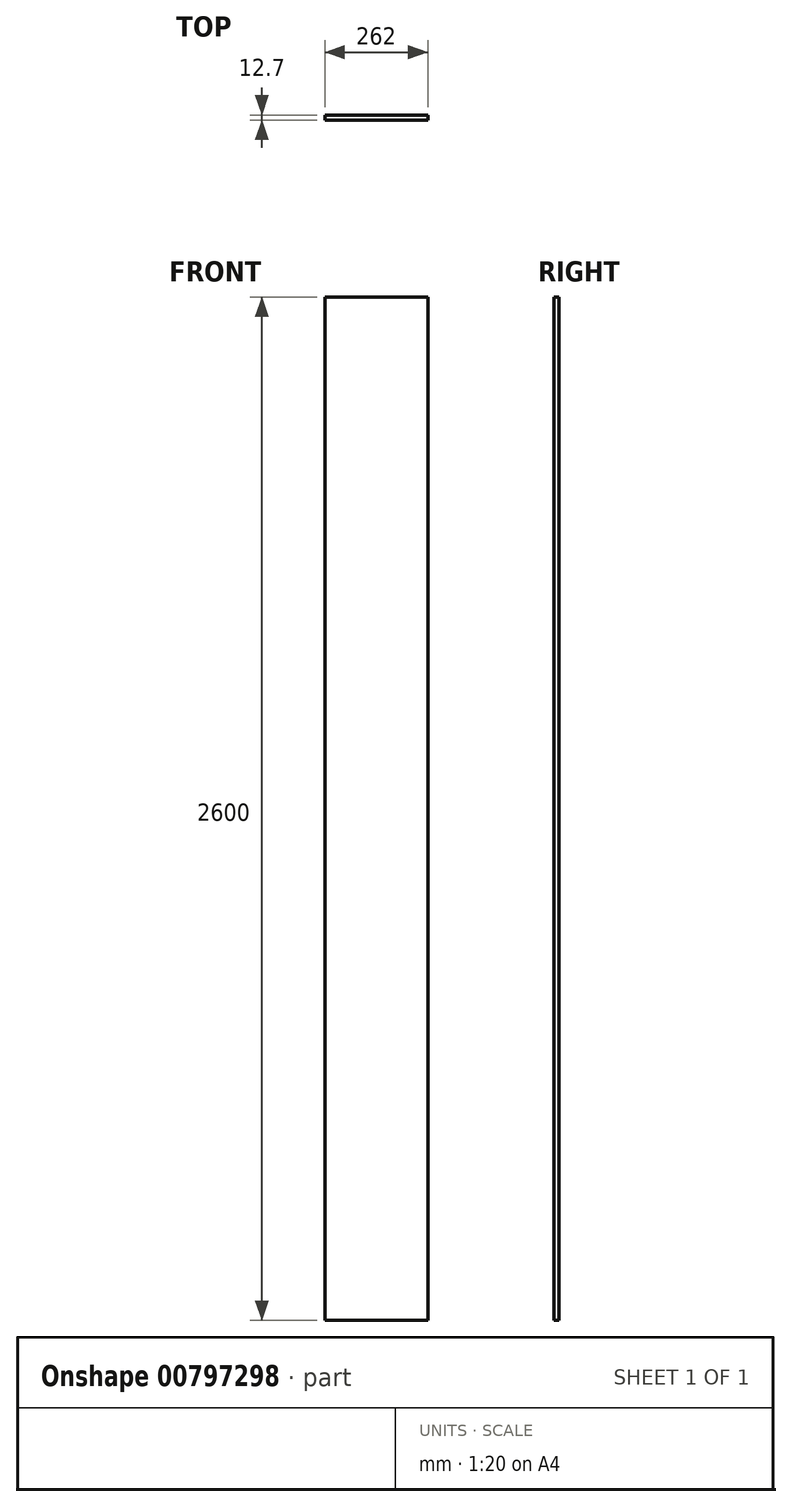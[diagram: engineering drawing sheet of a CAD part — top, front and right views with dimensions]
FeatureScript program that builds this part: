
annotation { "Feature Type Name" : "Feature", "Feature Type Description" : "" }
export const myFeature = defineFeature(function(context is Context, id is Id, definition is map)
    precondition{}
    {
        {
            var Q0;
            Q0=qCreatedBy(makeId("Front.planeOp"),FACE);
            var sketch = newSketch(context, id + "F0", { "sketchPlane" : qUnion([Q0])});
            skLineSegment(sketch, "E0.bottom", {"start": v(131, -1300) * mm, "end": v(-131, -1300) * mm});
            skLineSegment(sketch, "E0.top", {"start": v(131, 1300) * mm, "end": v(-131, 1300) * mm});
            skLineSegment(sketch, "E0.left", {"start": v(131, -1300) * mm, "end": v(131, 1300) * mm});
            skLineSegment(sketch, "E0.right", {"start": v(-131, -1300) * mm, "end": v(-131, 1300) * mm});
            skPoint(sketch, "E0.middle", {"position": v(0, 0) * mm});
            skSolve(sketch);
        }
        {
            var Q0;
            Q0 = qSketchRegion(id + "F0", true);
            extrude(context, id + "F1", {"entities" : qUnion([Q0]), "depth" : (25.4 / 2) * mm, "offsetDistance" : 25 * mm, "symmetric" : true});
        }
    });
